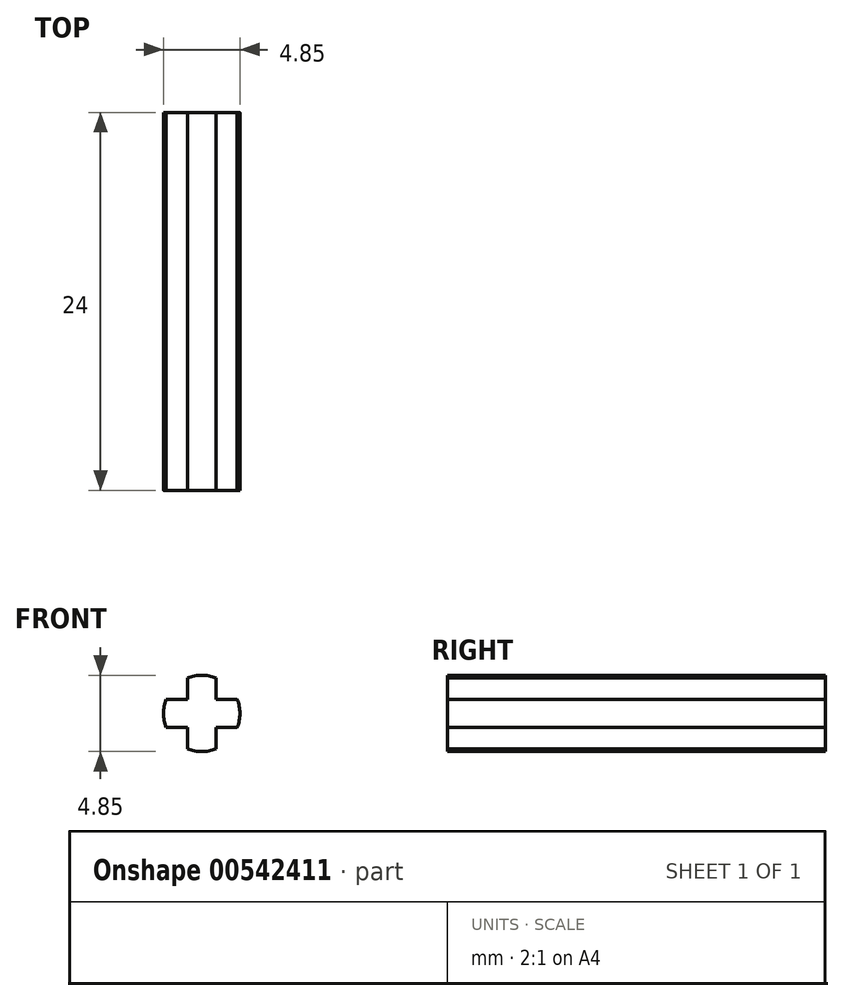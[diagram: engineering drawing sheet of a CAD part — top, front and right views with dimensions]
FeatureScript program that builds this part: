
annotation { "Feature Type Name" : "Feature", "Feature Type Description" : "" }
export const myFeature = defineFeature(function(context is Context, id is Id, definition is map)
    precondition{}
    {
        {
            var Q0;
            Q0=qCreatedBy(makeId("Front.planeOp"),FACE);
            var sketch = newSketch(context, id + "F0", { "sketchPlane" : qUnion([Q0])});
            skLineSegment(sketch, "E0", {"start": v(1.52, 0) * mm, "end": v(3.33, 0) * mm});
            skLineSegment(sketch, "E1", {"start": v(0, -3.33) * mm, "end": v(1.52, -3.32) * mm});
            skLineSegment(sketch, "E2", {"start": v(4.85, -1.52) * mm, "end": v(3.32, -1.52) * mm});
            skLineSegment(sketch, "E3", {"start": v(3.32, -4.85) * mm, "end": v(3.32, -3.32) * mm});
            skLineSegment(sketch, "E4", {"start": v(1.52, -4.85) * mm, "end": v(1.52, -3.32) * mm});
            skLineSegment(sketch, "E5.trimOffspring", {"start": v(1.52, -1.52) * mm, "end": v(0, -1.52) * mm});
            skLineSegment(sketch, "E6.trimOffspring", {"start": v(1.52, -1.52) * mm, "end": v(1.52, 0) * mm});
            skLineSegment(sketch, "E7.trimOffspring", {"start": v(3.32, -3.32) * mm, "end": v(4.85, -3.32) * mm});
            skLineSegment(sketch, "E8.trimOffspring", {"start": v(3.32, -1.52) * mm, "end": v(3.32, 0) * mm});
            skPoint(sketch, "E9.orphan", {"position": v(0, 0) * mm});
            skLineSegment(sketch, "E10", {"start": v(3.32, -4.85) * mm, "end": v(1.52, -4.85) * mm});
            skLineSegment(sketch, "E11", {"start": v(4.85, -1.52) * mm, "end": v(4.85, -3.32) * mm});
            skLineSegment(sketch, "E12", {"start": v(0, -1.52) * mm, "end": v(0, -3.33) * mm});
            skCircle(sketch, "E13", {"center": v(2.43, -2.43) * mm, "radius": 2.43 * mm});
            skSolve(sketch);
        }
        {
            var Q0;
            {var subQ4=sQuery(id+"F0.wireOp",EDGE,"E4");var subQ5=sQuery(id+"F0.wireOp",EDGE,"E1");var subQ6=makeQuery(id+"F0.imprint","INTERSECT",VERTEX,{"derivedFrom":[subQ5,subQ4]});Q0=makeQuery(id+"F0.imprint","IMPRINT",FACE,{"disambiguationData":[TD([[makeQuery(id+"F0.imprint","IMPRINT",EDGE,{"disambiguationData":[TD([[subQ6,1.0]])],"derivedFrom":subQ5}),1.0]])]});}
            extrude(context, id + "F1", {"entities" : qUnion([Q0]), "depth" : 24 * mm, "offsetDistance" : 25 * mm});
        }
    });
